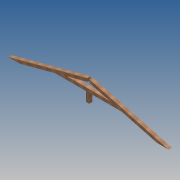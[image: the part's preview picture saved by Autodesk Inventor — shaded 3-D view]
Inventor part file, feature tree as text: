
AUTODESK INVENTOR PART (.ipt)
format: ipt  version: 2013 (Build 170138000, 138)  size: 94,208 bytes
history: native  units: in
note: dims shown in document units (in); Inventor stores cm internally (conversion verified against a paired STEP export)
features: extrude x1, sketch x1
ambient origin geometry x8: Origin, YZ Plane, XZ Plane, XY Plane, X Axis, Y Axis, Z Axis, Center Point
bodies: Solid1 (feature_tree)
feature tree (2):
  extrude  "Extrusion1"  TaperAngle=15.0deg  [1 undecoded]
  sketch  "Sketch1"  dims[d0=72.0in d1=15.0deg d2=5.5in d3=1.75in d4=10.0in d5=3.5in d6=3.5in d7=3.5in d8=0.0in]
note: 1 required parameter value undecoded (feature->parameter linkage not recoverable at this tier; creation-order binding heuristic only, values carry confidence <= 0.55)
